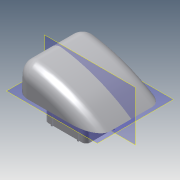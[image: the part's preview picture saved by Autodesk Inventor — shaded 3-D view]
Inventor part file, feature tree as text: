
AUTODESK INVENTOR PART (.ipt)
format: ipt  version: 2015 (Build 190159000, 159)  size: 418,816 bytes
history: native  units: in
note: dims shown in document units (in); Inventor stores cm internally (conversion verified against a paired STEP export)
features: extrude x5, sketch x5, projected_geometry x4, plane x3, mirror x2, fillet x1, shell x1, pattern_linear x1
ambient origin geometry x8: Origin, YZ Plane, XZ Plane, XY Plane, X Axis, Y Axis, Z Axis, Center Point
bodies: Body1 (feature_tree)
feature tree (22):
  extrude  "Extrusion2"  Depth=6.0in
  fillet  "Fillet2"  Radius=0.64in
  shell  "Shell1"  Thickness=6.0in
  plane  "Work Plane1"
  extrude  "Extrusion3"  Depth=6.0in
  extrude  "Extrusion4"  Depth=0.5in
  extrude  "Extrusion5"  TaperAngle=0.0deg  [1 undecoded]
  pattern_linear  "Rectangular Pattern1"  Spacing1=2.22in  [1 undecoded]
  plane  "Work Plane2"
  mirror  "Mirror1"
  extrude  "Extrusion6"  Depth=0.04in
  plane  "Work Plane3"
  mirror  "Mirror2"
  sketch  "Sketch4"  dims[d11=3.04in d14=3.01in d15=0.64in d17=6.0in]
  sketch  "Sketch5"  dims[d18=6.0in d19=0.4in]
  projected_geometry  "Projected Loop1"
  sketch  "Sketch6"  dims[d20=2.55in d21=0.0in d22=0.5in]
  projected_geometry  "Projected Loop2"
  sketch  "Sketch7"  dims[d23=0.07in d24=0.0in]
  projected_geometry  "Projected Loop3"
  sketch  "Sketch8"  dims[d25=0.68in d26=2.22in d27=0.29in d28=2.26in d29=0.15in d30=0.05in d31=2.55in d32=0.0in d33=0.67in d34=0.0in d35=0.05in d36=0.04in d37=0.925in d38=0.67in d39=0.0in d40=0.7874in d42=0.965in d43=0.04in d44=0.025in d45=0.025in d46=0.67in d47=0.0in]
  projected_geometry  "Projected Loop4"
note: 2 required parameter values undecoded (feature->parameter linkage not recoverable at this tier; creation-order binding heuristic only, values carry confidence <= 0.55)
